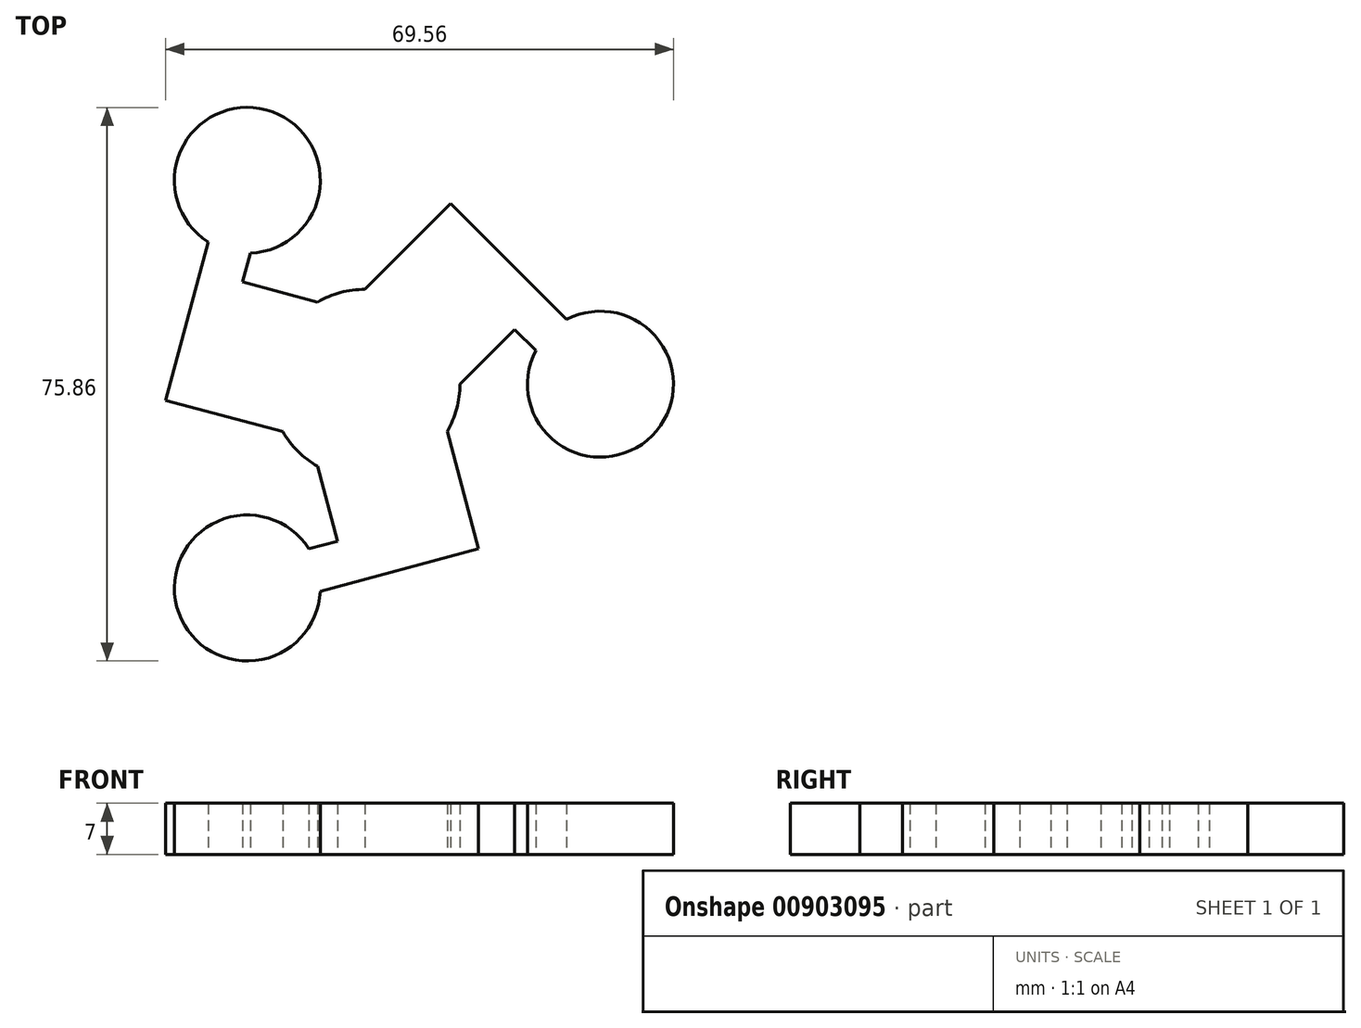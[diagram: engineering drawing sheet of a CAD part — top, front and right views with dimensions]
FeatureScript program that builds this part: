
annotation { "Feature Type Name" : "Feature", "Feature Type Description" : "" }
export const myFeature = defineFeature(function(context is Context, id is Id, definition is map)
    precondition{}
    {
        {
            var Q0;
            Q0=qCreatedBy(makeId("Top.planeOp"),FACE);
            var sketch = newSketch(context, id + "F0", { "sketchPlane" : qUnion([Q0])});
            skArc(sketch, "E0", {"start": v(0, 13) * mm, "mid": v(-3.36, 12.56) * mm, "end": v(-6.5, 11.26) * mm});
            skLineSegment(sketch, "E1", {"start": v(-13, 0) * mm, "end": v(13, 0) * mm, "construction": true});
            skLineSegment(sketch, "E2", {"start": v(0, 13) * mm, "end": v(11.75, 24.75) * mm});
            skLineSegment(sketch, "E3", {"start": v(13, 0) * mm, "end": v(20.5, 7.5) * mm});
            skLineSegment(sketch, "E4", {"start": v(11.75, 24.75) * mm, "end": v(27.63, 8.87) * mm});
            skPoint(sketch, "E5.positionSnap0", {"position": v(32.25, 0) * mm});
            skArc(sketch, "E6", {"start": v(23.39, 4.62) * mm, "mid": v(39.33, -7.07) * mm, "end": v(27.63, 8.87) * mm});
            skLineSegment(sketch, "E7.trimOffspring", {"start": v(20.5, 7.5) * mm, "end": v(23.39, 4.62) * mm});
            skPoint(sketch, "E8.orphan", {"position": v(30.13, -2.12) * mm});
            skPoint(sketch, "E9.orphan", {"position": v(34.38, 2.12) * mm});
            skLineSegment(sketch, "E10.1.0", {"start": v(-11.26, -6.5) * mm, "end": v(-27.3, -2.2) * mm});
            skLineSegment(sketch, "E10.1.1", {"start": v(-6.5, 11.26) * mm, "end": v(-16.75, 14) * mm});
            skLineSegment(sketch, "E10.1.2", {"start": v(-27.3, -2.2) * mm, "end": v(-21.5, 19.5) * mm});
            skLineSegment(sketch, "E10.1.3", {"start": v(-16.75, 14) * mm, "end": v(-15.7, 17.94) * mm});
            skArc(sketch, "E10.1.4", {"start": v(-15.7, 17.94) * mm, "mid": v(-13.54, 37.6) * mm, "end": v(-21.5, 19.5) * mm});
            skLineSegment(sketch, "E10.2.0", {"start": v(11.26, -6.5) * mm, "end": v(15.56, -22.55) * mm});
            skLineSegment(sketch, "E10.2.1", {"start": v(-6.5, -11.26) * mm, "end": v(-3.75, -21.51) * mm});
            skLineSegment(sketch, "E10.2.2", {"start": v(15.56, -22.55) * mm, "end": v(-6.14, -28.36) * mm});
            skLineSegment(sketch, "E10.2.3", {"start": v(-3.75, -21.51) * mm, "end": v(-7.69, -22.57) * mm});
            skArc(sketch, "E10.2.4", {"start": v(-7.69, -22.57) * mm, "mid": v(-25.79, -30.52) * mm, "end": v(-6.14, -28.36) * mm});
            skArc(sketch, "E11.trimOffspring", {"start": v(-11.26, -6.5) * mm, "mid": v(-9.2, -9.2) * mm, "end": v(-6.5, -11.26) * mm});
            skArc(sketch, "E12.trimOffspring", {"start": v(11.26, -6.5) * mm, "mid": v(12.56, -3.36) * mm, "end": v(13, 0) * mm});
            skSolve(sketch);
        }
        {
            var Q0;
            Q0 = qSketchRegion(id + "F0", true);
            extrude(context, id + "F1", {"entities" : qUnion([Q0]), "depth" : 7 * mm, "offsetDistance" : 25 * mm});
        }
    });
